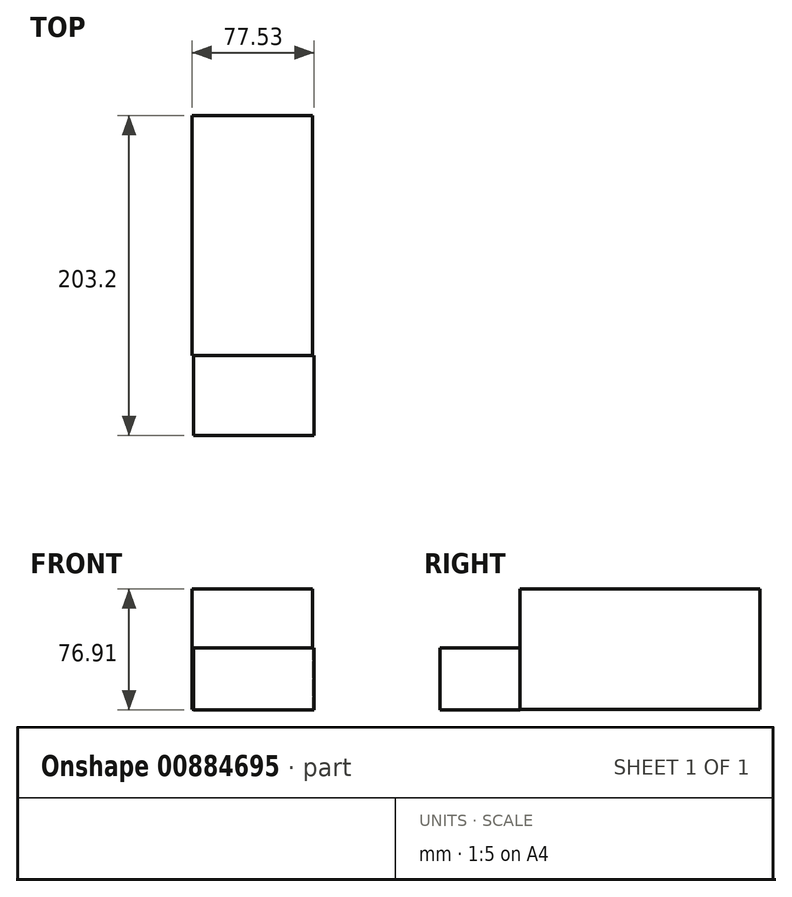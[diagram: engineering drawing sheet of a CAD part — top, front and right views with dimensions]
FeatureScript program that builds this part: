
annotation { "Feature Type Name" : "Feature", "Feature Type Description" : "" }
export const myFeature = defineFeature(function(context is Context, id is Id, definition is map)
    precondition{}
    {
        {
            var Q0;
            Q0=qCreatedBy(makeId("Front.planeOp"),FACE);
            var sketch = newSketch(context, id + "F0", { "sketchPlane" : qUnion([Q0])});
            skLineSegment(sketch, "E0.bottom", {"start": v(-26.83, 30.24) * mm, "end": v(49.77, 30.24) * mm});
            skLineSegment(sketch, "E0.top", {"start": v(-26.83, -46.36) * mm, "end": v(49.77, -46.36) * mm});
            skLineSegment(sketch, "E0.left", {"start": v(-26.83, 30.24) * mm, "end": v(-26.83, -46.36) * mm});
            skLineSegment(sketch, "E0.right", {"start": v(49.77, 30.24) * mm, "end": v(49.77, -46.36) * mm});
            skSolve(sketch);
        }
        {
            var Q0;
            Q0 = qSketchRegion(id + "F0", true);
            extrude(context, id + "F1", {"entities" : qUnion([Q0]), "oppositeDirection" : true, "depth" : 152.4 * mm, "offsetDistance" : 25.4 * mm});
        }
        {
            var Q0;
            Q0=qCreatedBy(makeId("Front.planeOp"),FACE);
            var sketch = newSketch(context, id + "F2", { "sketchPlane" : qUnion([Q0])});
            skLineSegment(sketch, "E1.bottom", {"start": v(-25.9, -7.29) * mm, "end": v(50.7, -7.29) * mm});
            skLineSegment(sketch, "E1.top", {"start": v(-25.9, -46.67) * mm, "end": v(50.7, -46.67) * mm});
            skLineSegment(sketch, "E1.left", {"start": v(-25.9, -7.29) * mm, "end": v(-25.9, -46.67) * mm});
            skLineSegment(sketch, "E1.right", {"start": v(50.7, -7.29) * mm, "end": v(50.7, -46.67) * mm});
            skSolve(sketch);
        }
        {
            var Q0;
            Q0 = qSketchRegion(id + "F2", true);
            extrude(context, id + "F3", {"entities" : qUnion([Q0]), "operationType" : NewBodyOperationType.ADD, "depth" : 50.8 * mm, "offsetDistance" : 25.4 * mm});
        }
    });
